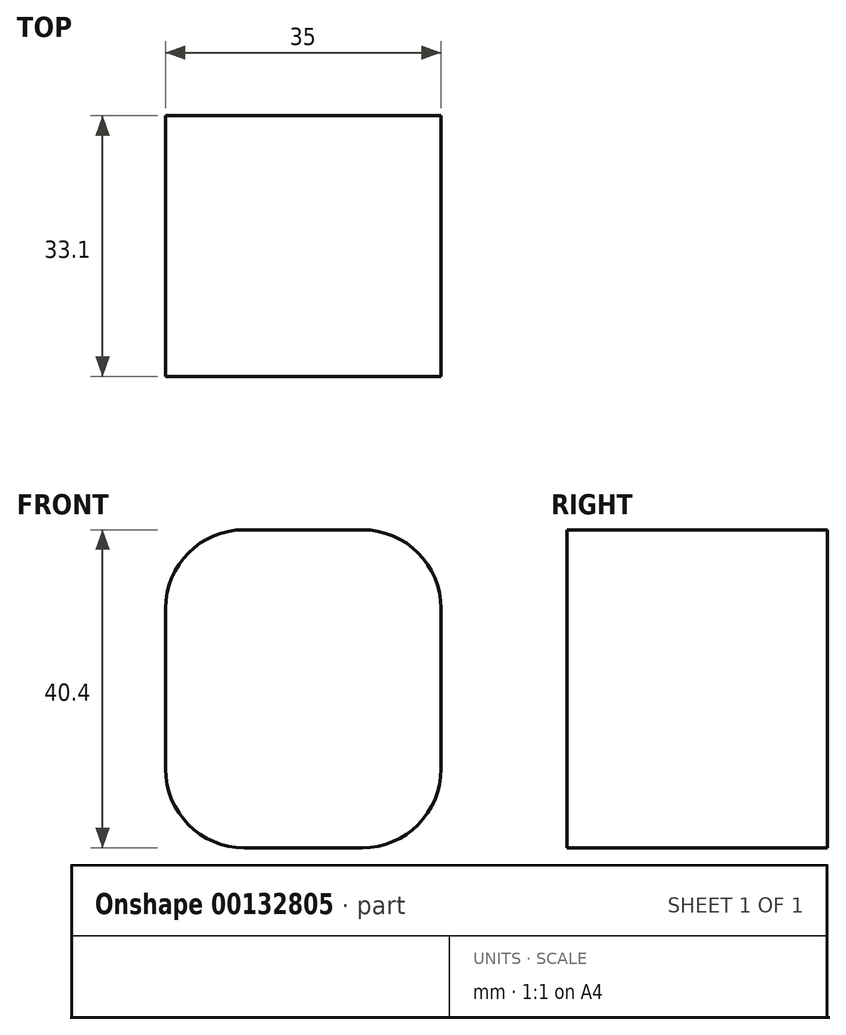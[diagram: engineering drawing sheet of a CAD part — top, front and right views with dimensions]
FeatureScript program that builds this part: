
annotation { "Feature Type Name" : "Feature", "Feature Type Description" : "" }
export const myFeature = defineFeature(function(context is Context, id is Id, definition is map)
    precondition{}
    {
        {
            var Q0;
            Q0=qCreatedBy(makeId("Front.planeOp"),FACE);
            var sketch = newSketch(context, id + "F0", { "sketchPlane" : qUnion([Q0])});
            skLineSegment(sketch, "E0.bottom", {"start": v(-7.5, 2) * mm, "end": v(7.5, 2) * mm});
            skLineSegment(sketch, "E0.top", {"start": v(-7.5, 42.4) * mm, "end": v(7.5, 42.4) * mm});
            skLineSegment(sketch, "E0.left", {"start": v(-17.5, 12) * mm, "end": v(-17.5, 32.4) * mm});
            skLineSegment(sketch, "E0.right", {"start": v(17.5, 12) * mm, "end": v(17.5, 32.4) * mm});
            skArc(sketch, "E1.filletArc", {"start": v(-7.5, 42.4) * mm, "mid": v(-14.57, 39.47) * mm, "end": v(-17.5, 32.4) * mm});
            skArc(sketch, "E2.filletArc", {"start": v(17.5, 32.4) * mm, "mid": v(14.57, 39.47) * mm, "end": v(7.5, 42.4) * mm});
            skArc(sketch, "E3.filletArc", {"start": v(7.5, 2) * mm, "mid": v(14.57, 4.93) * mm, "end": v(17.5, 12) * mm});
            skArc(sketch, "E4.filletArc", {"start": v(-17.5, 12) * mm, "mid": v(-14.57, 4.93) * mm, "end": v(-7.5, 2) * mm});
            skSolve(sketch);
        }
        {
            var Q0;
            Q0=makeQuery(id+"F0.imprint","IMPRINT",FACE,{"disambiguationData":[TD([[makeQuery(id+"F0.imprint","IMPRINT",EDGE,{"derivedFrom":sQuery(id+"F0.wireOp",EDGE,"E0.bottom")}),1.0]])]});
            extrude(context, id + "F1", {"entities" : qUnion([Q0]), "endBound" : BoundingType.SYMMETRIC, "depth" : 33.1 * mm});
        }
    });
